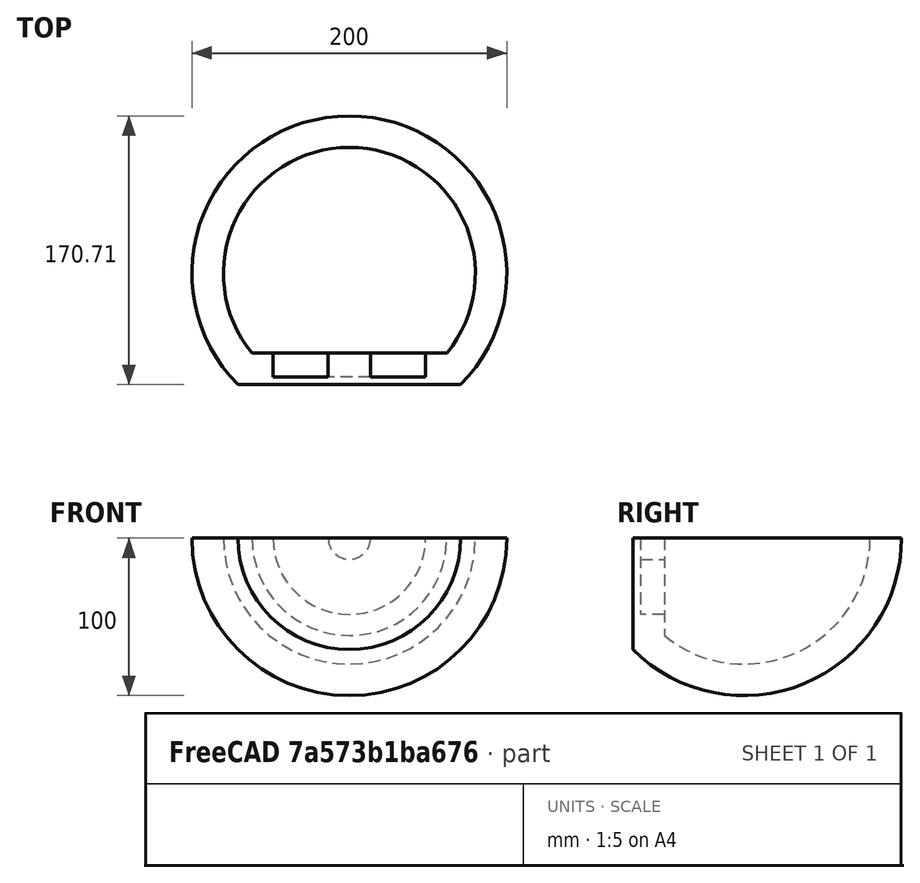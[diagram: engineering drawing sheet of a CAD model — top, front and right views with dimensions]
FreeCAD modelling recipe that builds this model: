
FCSTD DOCUMENT  (FreeCAD 0.18R4 (GitTag))
Label: Ariel Half
License: All rights reserved
LicenseURL: http://en.wikipedia.org/wiki/All_rights_reserved
objects: Sketcher::SketchObject×2, PartDesign::Revolution×1, PartDesign::Body×1
note: 5 computed .brp shape members not serialized (recipe doc carries the construction recipe); baked Part::Feature solids carry a one-line shape summary decoded from their .brp

FEATURE [Sketcher::SketchObject] Sketch
  sketch-geometry (16):
    g0: ArcOfCircle CenterX=0 CenterY=0 CenterZ=0 NormalX=0 NormalY=0 NormalZ=1 AngleXU=0 Radius=100 StartAngle=5.49779 EndAngle=7.85398
    g1: LineSegment StartX=3.06e-14 StartY=100 StartZ=0 EndX=2.43e-14 EndY=80 EndZ=0
    g2: LineSegment [constr] StartX=0 StartY=0 StartZ=0 EndX=106.066 EndY=-106.066 EndZ=0
    g3: LineSegment StartX=70.7107 StartY=-70.7107 StartZ=0 EndX=0 EndY=-70.7107 EndZ=0
    g4: LineSegment StartX=61.8743 StartY=-50.7107 StartZ=0 EndX=48.4371 EndY=-50.7107 EndZ=0
    g5: LineSegment StartX=48.4371 StartY=-50.7107 StartZ=0 EndX=48.4371 EndY=-65.7107 EndZ=0
    g6: LineSegment StartX=48.4371 StartY=-65.7107 StartZ=0 EndX=13.4371 EndY=-65.7107 EndZ=0
    g7: LineSegment StartX=13.4371 StartY=-65.7107 StartZ=0 EndX=13.4371 EndY=-50.7107 EndZ=0
    g8: LineSegment StartX=13.4371 StartY=-50.7107 StartZ=0 EndX=0 EndY=-50.7107 EndZ=0
    g9: LineSegment StartX=0 StartY=-50.7107 StartZ=0 EndX=0 EndY=-70.7107 EndZ=0
    g10: ArcOfCircle CenterX=-2e-16 CenterY=-8.2e-15 CenterZ=0 NormalX=0 NormalY=0 NormalZ=1 AngleXU=0 Radius=80 StartAngle=5.59662 EndAngle=7.85398
    g11: LineSegment [constr] StartX=0 StartY=0 StartZ=0 EndX=106.066 EndY=106.066 EndZ=0
    g12: GeomPoint X=56.5685 Y=56.5685 Z=0
    g13: GeomPoint X=70.7107 Y=70.7107 Z=0
    g14: GeomPoint X=100 Y=0 Z=0
    g15: GeomPoint X=80 Y=0 Z=0
  constraints (44):
    c: Coincident(g0,g-1)
    c: PointOnObject(g0,g-2)
    c: Radius(g0) = 100
    c: PointOnObject(g1,g-2)
    c: DistanceY(g1,g0) = 20
    c: Coincident(g1,g0)
    c: Coincident(g2,g0)
    c: Angle(g2,g-1) = 0.785398
    c: Distance(g2) = 150
    c: PointOnObject(g0,g2)
    c: Coincident(g3,g0)
    c: PointOnObject(g3,g-2)
    c: Horizontal(g3)
    c: Horizontal(g4)
    c: Coincident(g5,g4)
    c: Vertical(g5)
    c: Coincident(g6,g5)
    c: Horizontal(g6)
    c: Coincident(g7,g6)
    c: Vertical(g7)
    c: Coincident(g8,g7)
    c: PointOnObject(g8,g-2)
    c: Coincident(g9,g8)
    c: Coincident(g9,g3)
    c: DistanceX(g6,g6) = 35
    c: Horizontal(g8,g4)
    c: Horizontal(g8)
    c: DistanceY(g3,g6) = 5
    c: Equal(g1,g9)
    c: Coincident(g10,g1)
    c: Coincident(g10,g4)
    c: Coincident(g11,g0)
    c: Symmetric(g11,g2,g-1)
    c: PointOnObject(g12,g10)
    c: PointOnObject(g13,g0)
    c: PointOnObject(g12,g11)
    c: PointOnObject(g13,g11)
    c: Distance(g13,g12) = 20
    c: PointOnObject(g14,g0)
    c: PointOnObject(g15,g10)
    c: PointOnObject(g15,g-1)
    c: PointOnObject(g14,g-1)
    c: Distance(g15,g14) = 20
    c: Equal(g4,g8)
FEATURE [PartDesign::Revolution] Revolution
  Angle = 180
  Axis = (0,1,0)
  Base = (0,0,0)
  Profile = -> Sketch
  ReferenceAxis = -> Sketch [V_Axis]
FEATURE [Sketcher::SketchObject] Sketch001
  MapMode = 5
  Support = -> [XY_Plane]
FEATURE [PartDesign::Body] Body
  Group = -> [Sketch,Revolution,Sketch001]
  Origin = -> Origin
  Tip = -> Revolution
